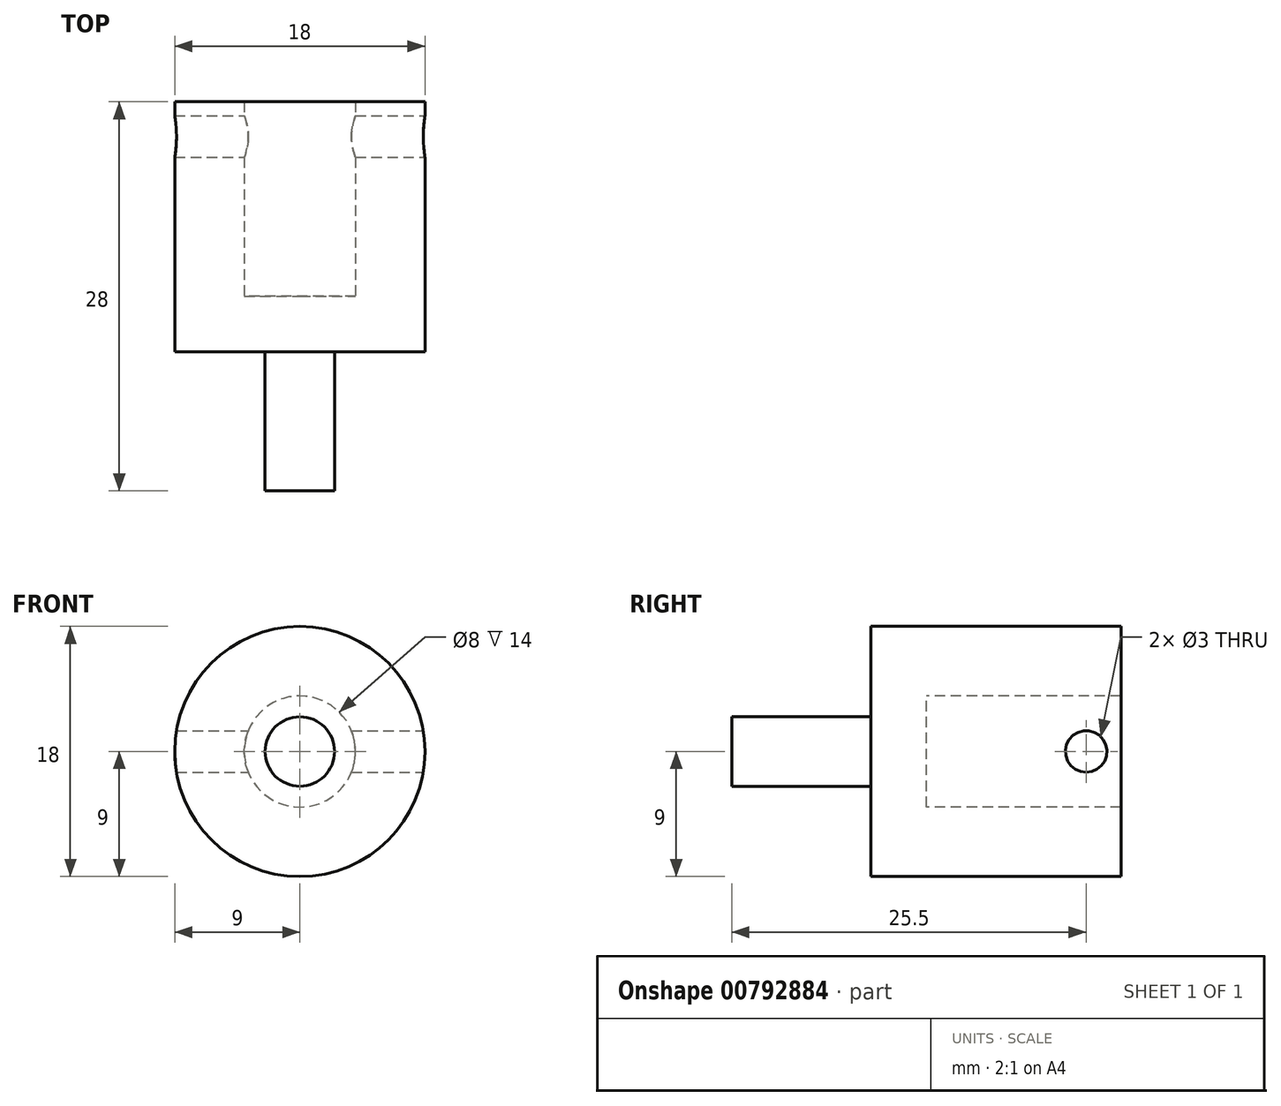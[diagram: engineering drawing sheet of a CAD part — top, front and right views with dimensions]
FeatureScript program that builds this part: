
annotation { "Feature Type Name" : "Feature", "Feature Type Description" : "" }
export const myFeature = defineFeature(function(context is Context, id is Id, definition is map)
    precondition{}
    {
        {
            var Q0;
            Q0=qCreatedBy(makeId("Front.planeOp"),FACE);
            var sketch = newSketch(context, id + "F0", { "sketchPlane" : qUnion([Q0])});
            skCircle(sketch, "E0", {"center": v(0, 0) * mm, "radius": 2.5 * mm});
            skSolve(sketch);
        }
        {
            var Q0;
            Q0 = qSketchRegion(id + "F0", true);
            extrude(context, id + "F1", {"entities" : qUnion([Q0]), "depth" : 10 * mm, "offsetDistance" : 25.4 * mm});
        }
        {
            var Q0;
            Q0=qCreatedBy(makeId("Front.planeOp"),FACE);
            var sketch = newSketch(context, id + "F2", { "sketchPlane" : qUnion([Q0])});
            skCircle(sketch, "E1", {"center": v(0, 0) * mm, "radius": 9 * mm});
            skSolve(sketch);
        }
        {
            var Q0;
            Q0 = qSketchRegion(id + "F2", true);
            extrude(context, id + "F3", {"entities" : qUnion([Q0]), "operationType" : NewBodyOperationType.ADD, "oppositeDirection" : true, "depth" : 18 * mm, "offsetDistance" : 25.4 * mm});
        }
        {
            var Q0;
            Q0=qCreatedBy(makeId("Front.planeOp"),FACE);
            var sketch = newSketch(context, id + "F4", { "sketchPlane" : qUnion([Q0])});
            skCircle(sketch, "E2", {"center": v(0, 0) * mm, "radius": 4 * mm});
            skSolve(sketch);
        }
        {
            var Q0;
            Q0=makeQuery(id+"F4.imprint","IMPRINT",FACE,{"disambiguationData":[TD([[makeQuery(id+"F4.imprint","IMPRINT",EDGE,{"derivedFrom":sQuery(id+"F4.wireOp",EDGE,"E2")}),1.0]])]});
            extrude(context, id + "F5", {"entities" : qUnion([Q0]), "operationType" : NewBodyOperationType.REMOVE, "oppositeDirection" : true, "depth" : 25.4 * mm, "offsetDistance" : 25.4 * mm, "hasSecondDirection" : true, "secondDirectionOppositeDirection" : true, "secondDirectionDepth" : 4 * mm});
        }
        {
            var Q0;
            Q0=qCreatedBy(makeId("Right.planeOp"),FACE);
            var sketch = newSketch(context, id + "F6", { "sketchPlane" : qUnion([Q0])});
            skCircle(sketch, "E3", {"center": v(15.5, 0) * mm, "radius": 1.5 * mm});
            skSolve(sketch);
        }
        {
            var Q0;
            Q0 = qSketchRegion(id + "F6", true);
            extrude(context, id + "F7", {"entities" : qUnion([Q0]), "operationType" : NewBodyOperationType.REMOVE, "oppositeDirection" : true, "depth" : 25.4 * mm, "offsetDistance" : 25.4 * mm, "hasSecondDirection" : true, "secondDirectionOppositeDirection" : false, "secondDirectionDepth" : 32 * mm});
        }
    });
